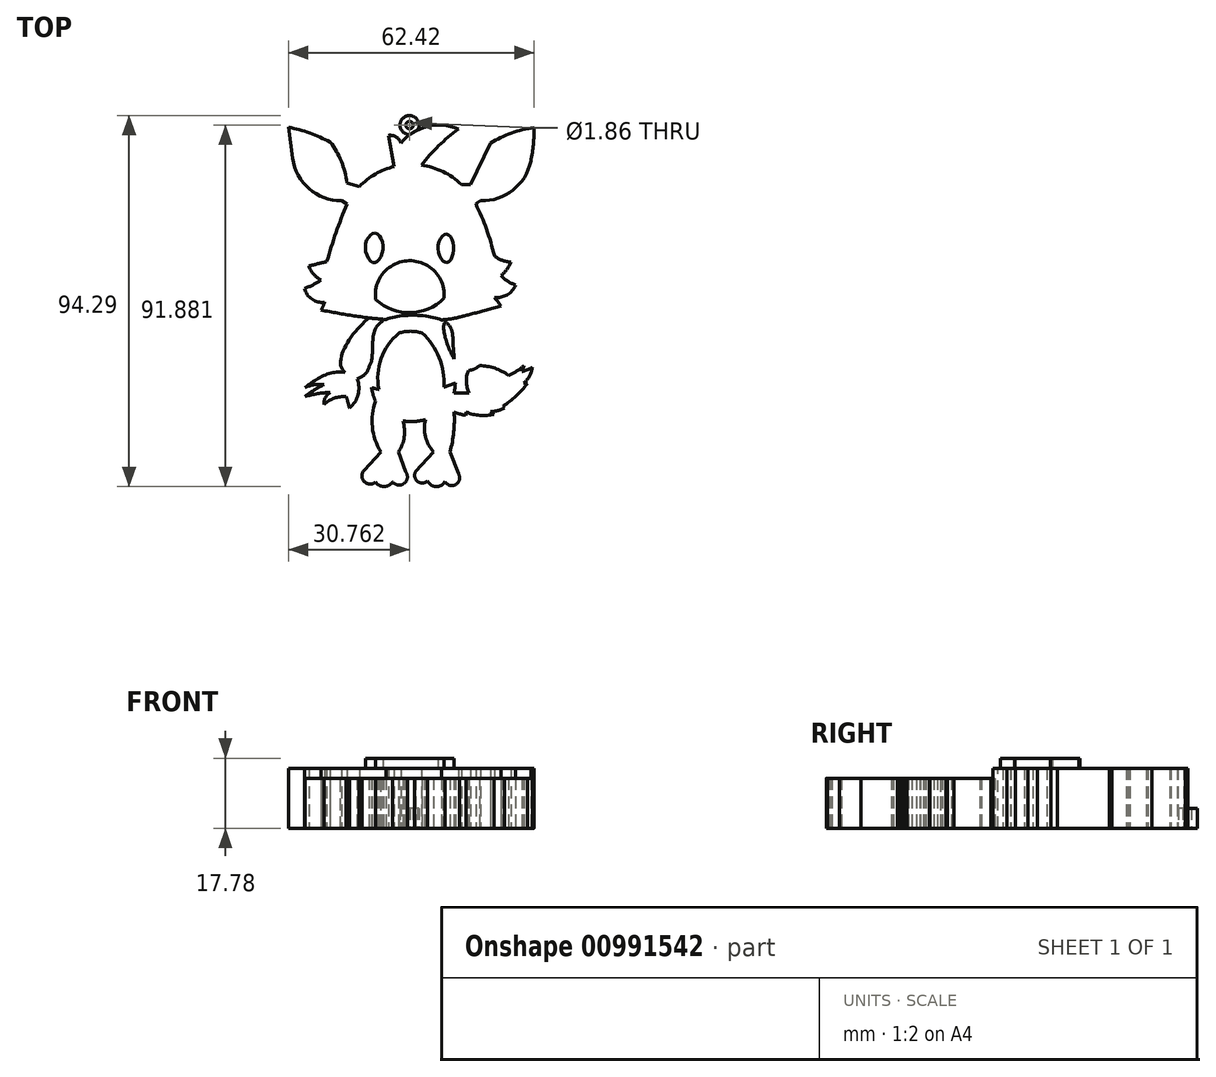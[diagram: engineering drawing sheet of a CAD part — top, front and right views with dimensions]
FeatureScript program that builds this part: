
annotation { "Feature Type Name" : "Feature", "Feature Type Description" : "" }
export const myFeature = defineFeature(function(context is Context, id is Id, definition is map)
    precondition{}
    {
        {
            var Q0;
            Q0=qCreatedBy(makeId("Top.planeOp"),FACE);
            var sketch = newSketch(context, id + "F0", { "sketchPlane" : qUnion([Q0])});
            skLineSegment(sketch, "E0.bottom", {"start": v(-53.94, 80.3) * mm, "end": v(50.51, 80.3) * mm});
            skLineSegment(sketch, "E0.top", {"start": v(-53.94, -54.97) * mm, "end": v(50.51, -54.97) * mm});
            skLineSegment(sketch, "E0.left", {"start": v(-53.94, 80.3) * mm, "end": v(-53.94, -54.97) * mm});
            skLineSegment(sketch, "E0.right", {"start": v(50.51, 80.3) * mm, "end": v(50.51, -54.97) * mm});
            skSolve(sketch);
        }
        {
            var Q0;
            Q0 = qSketchRegion(id + "F0", true);
            extrude(context, id + "F1", {"entities" : qUnion([Q0]), "depth" : 2.54 * mm, "offsetDistance" : 25.4 * mm});
        }
        {
            var Q0;
            Q0=makeQuery(id+"F1.opExtrude","CAP_FACE",FACE,{"disambiguationData":[OSD([sQuery(id+"F0.wireOp",EDGE,"E0.bottom"),sQuery(id+"F0.wireOp",EDGE,"E0.top"),sQuery(id+"F0.wireOp",EDGE,"E0.left"),sQuery(id+"F0.wireOp",EDGE,"E0.right")])],"isStart":false});
            var sketch = newSketch(context, id + "F2", { "sketchPlane" : qUnion([Q0])});
            skLineSegment(sketch, "E1", {"start": v(-10.19, 52.9) * mm, "end": v(-8.72, 45) * mm});
            skArc(sketch, "E2", {"start": v(-6.98, 50.92) * mm, "mid": v(-8.22, 52.5) * mm, "end": v(-10.19, 52.9) * mm});
            skArc(sketch, "E3", {"start": v(7.56, 54.5) * mm, "mid": v(-0.32, 55.19) * mm, "end": v(-6.98, 50.92) * mm});
            skArc(sketch, "E4", {"start": v(7.56, 54.5) * mm, "mid": v(2.55, 50.26) * mm, "end": v(-1.81, 45.35) * mm});
            skArc(sketch, "E5", {"start": v(12, 35.53) * mm, "mid": v(6.3, 42.13) * mm, "end": v(-1.81, 45.35) * mm});
            skArc(sketch, "E6.trimOffspring", {"start": v(-8.72, 45) * mm, "mid": v(-15.79, 41.54) * mm, "end": v(-20.76, 35.43) * mm});
            skLineSegment(sketch, "E7", {"start": v(-20.76, 35.43) * mm, "end": v(-22.08, 36.28) * mm});
            skLineSegment(sketch, "E8", {"start": v(-22.08, 36.28) * mm, "end": v(-20.76, 40.82) * mm});
            skLineSegment(sketch, "E9", {"start": v(-20.76, 40.82) * mm, "end": v(-17.6, 39.9) * mm});
            skLineSegment(sketch, "E10", {"start": v(12, 35.53) * mm, "end": v(13.22, 36.28) * mm});
            skLineSegment(sketch, "E11", {"start": v(13.22, 36.28) * mm, "end": v(10.66, 40.46) * mm});
            skLineSegment(sketch, "E12", {"start": v(10.66, 40.46) * mm, "end": v(8.32, 40.46) * mm});
            skArc(sketch, "E13", {"start": v(-34.54, 47.14) * mm, "mid": v(-30.35, 39.37) * mm, "end": v(-22.08, 36.28) * mm});
            skLineSegment(sketch, "E14", {"start": v(-34.54, 47.14) * mm, "end": v(-35.6, 54.98) * mm});
            skArc(sketch, "E15", {"start": v(-25, 51.2) * mm, "mid": v(-30.16, 53.5) * mm, "end": v(-35.6, 54.98) * mm});
            skArc(sketch, "E16", {"start": v(-20.76, 40.82) * mm, "mid": v(-22.16, 46.3) * mm, "end": v(-25, 51.2) * mm});
            skLineSegment(sketch, "E17", {"start": v(10.66, 40.46) * mm, "end": v(15.68, 50.92) * mm});
            skArc(sketch, "E18", {"start": v(26.82, 54.88) * mm, "mid": v(21.04, 53.48) * mm, "end": v(15.68, 50.92) * mm});
            skArc(sketch, "E19", {"start": v(25.97, 46.38) * mm, "mid": v(26.64, 50.6) * mm, "end": v(26.82, 54.88) * mm});
            skArc(sketch, "E20", {"start": v(13.22, 36.28) * mm, "mid": v(21.44, 39) * mm, "end": v(25.97, 46.38) * mm});
            skArc(sketch, "E21", {"start": v(-30.86, 44.4) * mm, "mid": v(-27.6, 39.12) * mm, "end": v(-21.42, 38.55) * mm});
            skLineSegment(sketch, "E22", {"start": v(-30.86, 44.4) * mm, "end": v(-32.84, 51.2) * mm});
            skArc(sketch, "E23", {"start": v(-25.1, 48.84) * mm, "mid": v(-28.77, 50.69) * mm, "end": v(-32.84, 51.2) * mm});
            skArc(sketch, "E24", {"start": v(-21.14, 39.5) * mm, "mid": v(-22.52, 44.43) * mm, "end": v(-25.1, 48.84) * mm});
            skLineSegment(sketch, "E25", {"start": v(11.32, 39.37) * mm, "end": v(16.43, 48.93) * mm});
            skArc(sketch, "E26", {"start": v(23.89, 51.58) * mm, "mid": v(19.93, 50.9) * mm, "end": v(16.43, 48.93) * mm});
            skLineSegment(sketch, "E27", {"start": v(23.89, 51.58) * mm, "end": v(21.15, 41.38) * mm});
            skArc(sketch, "E28", {"start": v(12.5, 37.45) * mm, "mid": v(17.43, 38.09) * mm, "end": v(21.15, 41.38) * mm});
            skLineSegment(sketch, "E29", {"start": v(-1.94, 54.66) * mm, "end": v(-1.94, 52.52) * mm});
            skLineSegment(sketch, "E30", {"start": v(-1.94, 52.52) * mm, "end": v(-1.03, 52.52) * mm});
            skLineSegment(sketch, "E31", {"start": v(-1.03, 52.52) * mm, "end": v(-1.03, 51.2) * mm});
            skLineSegment(sketch, "E32", {"start": v(-1.03, 51.2) * mm, "end": v(0, 51.2) * mm});
            skLineSegment(sketch, "E33", {"start": v(0, 51.2) * mm, "end": v(0, 49.88) * mm});
            skLineSegment(sketch, "E34", {"start": v(0, 49.88) * mm, "end": v(2.16, 49.88) * mm});
            skArc(sketch, "E35", {"start": v(-20.76, 35.43) * mm, "mid": v(-23.5, 28.19) * mm, "end": v(-25.86, 20.8) * mm});
            skArc(sketch, "E36", {"start": v(16.72, 22.31) * mm, "mid": v(14.72, 29.05) * mm, "end": v(12, 35.53) * mm});
            skArc(sketch, "E37", {"start": v(-25.86, 20.8) * mm, "mid": v(-28.14, 20.28) * mm, "end": v(-30.41, 19.73) * mm});
            skArc(sketch, "E38", {"start": v(-30.41, 19.73) * mm, "mid": v(-29.2, 17.62) * mm, "end": v(-27.27, 16.14) * mm});
            skArc(sketch, "E39", {"start": v(-31.53, 14) * mm, "mid": v(-29.33, 14.94) * mm, "end": v(-27.27, 16.14) * mm});
            skArc(sketch, "E40", {"start": v(-31.53, 14) * mm, "mid": v(-29.63, 11.27) * mm, "end": v(-26.37, 10.53) * mm});
            skArc(sketch, "E41", {"start": v(-27.27, 8.5) * mm, "mid": v(-26.78, 9.5) * mm, "end": v(-26.37, 10.53) * mm});
            skArc(sketch, "E42", {"start": v(16.72, 22.31) * mm, "mid": v(18.67, 21.18) * mm, "end": v(20.89, 20.74) * mm});
            skArc(sketch, "E43", {"start": v(18.42, 17.26) * mm, "mid": v(19.87, 18.85) * mm, "end": v(20.89, 20.74) * mm});
            skArc(sketch, "E44", {"start": v(18.42, 17.26) * mm, "mid": v(20.12, 15.85) * mm, "end": v(22.12, 14.9) * mm});
            skArc(sketch, "E45", {"start": v(16.72, 11.76) * mm, "mid": v(19.97, 12.38) * mm, "end": v(22.12, 14.9) * mm});
            skArc(sketch, "E46", {"start": v(18.42, 9.52) * mm, "mid": v(17.6, 10.66) * mm, "end": v(16.72, 11.76) * mm});
            skFitSpline(sketch, "E47", {"points": [v(-13.57, 28.04) * mm, v(-16.04, 24.9) * mm, v(-13.9, 20.52) * mm, v(-11.55, 24.22) * mm, v(-13.57, 28.04) * mm]});
            skFitSpline(sketch, "E48", {"points": [v(2.37, 24.11) * mm, v(4.5, 27.82) * mm, v(6.4, 24.22) * mm, v(4.61, 20.63) * mm, v(2.37, 24.11) * mm]});
            skArc(sketch, "E49", {"start": v(3.94, 11.54) * mm, "mid": v(-4.95, 21.06) * mm, "end": v(-13.46, 11.2) * mm});
            skArc(sketch, "E50", {"start": v(-13.46, 11.2) * mm, "mid": v(-4.7, 7.88) * mm, "end": v(3.94, 11.54) * mm});
            skArc(sketch, "E51", {"start": v(-9.17, 19.87) * mm, "mid": v(-5.03, 16.55) * mm, "end": v(-1.3, 20.33) * mm});
            skFitSpline(sketch, "E52", {"points": [v(-11.99, 5.47) * mm, v(-14.25, -1.59) * mm, v(-14.72, -8.57) * mm, v(-12.26, -16.6) * mm, v(-4.14, -19.8) * mm, v(4.92, -15.93) * mm, v(6.8, -8.19) * mm, v(6.24, 0) * mm, v(4.25, 5.49) * mm, v(-11.99, 5.47) * mm]});
            skArc(sketch, "E53", {"start": v(6.24, 0) * mm, "mid": v(5.33, 2.77) * mm, "end": v(4.25, 5.49) * mm});
            skFitSpline(sketch, "E54", {"points": [v(9.21, 6.25) * mm, v(11.66, 2.06) * mm, v(13.79, -4.3) * mm, v(10.1, -6.8) * mm, v(6.53, -3.96) * mm, v(4.25, 5.49) * mm, v(8.1, 6.04) * mm, v(9.21, 6.25) * mm]});
            skArc(sketch, "E55", {"start": v(-26.54, -10.42) * mm, "mid": v(-29.04, -10.45) * mm, "end": v(-31.43, -11.15) * mm});
            skArc(sketch, "E56", {"start": v(-26.54, -10.42) * mm, "mid": v(-29.08, -11.8) * mm, "end": v(-31.43, -13.47) * mm});
            skArc(sketch, "E57", {"start": v(-24.97, -12.4) * mm, "mid": v(-28.23, -12.74) * mm, "end": v(-31.43, -13.47) * mm});
            skArc(sketch, "E58", {"start": v(-24.97, -12.4) * mm, "mid": v(-26.21, -13.67) * mm, "end": v(-26.54, -15.41) * mm});
            skArc(sketch, "E59", {"start": v(-20.93, -13.47) * mm, "mid": v(-23.94, -13.87) * mm, "end": v(-26.54, -15.41) * mm});
            skArc(sketch, "E60", {"start": v(-20.1, -16.4) * mm, "mid": v(-20.47, -14.92) * mm, "end": v(-20.93, -13.47) * mm});
            skArc(sketch, "E61", {"start": v(-20.1, -16.4) * mm, "mid": v(-17.93, -13) * mm, "end": v(-18.13, -8.98) * mm});
            skArc(sketch, "E62", {"start": v(10.1, -6.8) * mm, "mid": v(9.74, -10.83) * mm, "end": v(11.68, -14.36) * mm});
            skArc(sketch, "E63", {"start": v(12.52, -11.62) * mm, "mid": v(12.09, -13) * mm, "end": v(11.68, -14.36) * mm});
            skArc(sketch, "E64", {"start": v(17.9, -13.47) * mm, "mid": v(15.29, -12.33) * mm, "end": v(12.52, -11.62) * mm});
            skArc(sketch, "E65", {"start": v(17.9, -13.47) * mm, "mid": v(17.15, -12.02) * mm, "end": v(15.77, -11.15) * mm});
            skArc(sketch, "E66", {"start": v(22, -12.4) * mm, "mid": v(18.94, -11.5) * mm, "end": v(15.77, -11.15) * mm});
            skArc(sketch, "E67", {"start": v(22, -12.4) * mm, "mid": v(20.23, -10.3) * mm, "end": v(17.82, -8.98) * mm});
            skArc(sketch, "E68", {"start": v(22, -9.6) * mm, "mid": v(19.95, -9.03) * mm, "end": v(17.82, -8.98) * mm});
            skArc(sketch, "E69", {"start": v(22, -9.6) * mm, "mid": v(17.87, -6.66) * mm, "end": v(12.92, -5.6) * mm});
            skLineSegment(sketch, "E70", {"start": v(6.48, -12.55) * mm, "end": v(10.35, -12.55) * mm});
            skArc(sketch, "E71", {"start": v(20.33, -8.1) * mm, "mid": v(22.39, -7.01) * mm, "end": v(24.25, -5.62) * mm});
            skArc(sketch, "E72", {"start": v(23.8, -7.08) * mm, "mid": v(25.15, -6.64) * mm, "end": v(26.38, -5.95) * mm});
            skArc(sketch, "E73", {"start": v(24.13, -10.05) * mm, "mid": v(25.64, -8.21) * mm, "end": v(26.38, -5.95) * mm});
            skArc(sketch, "E74", {"start": v(18.86, -15.89) * mm, "mid": v(22.23, -13.3) * mm, "end": v(25.09, -10.16) * mm});
            skArc(sketch, "E75", {"start": v(15.72, -17.3) * mm, "mid": v(17.54, -17.03) * mm, "end": v(19.25, -16.34) * mm});
            skArc(sketch, "E76", {"start": v(9.54, -17.4) * mm, "mid": v(13.06, -18.24) * mm, "end": v(16.67, -17.96) * mm});
            skArc(sketch, "E77", {"start": v(6.45, -17.4) * mm, "mid": v(7.98, -17.9) * mm, "end": v(9.54, -18.22) * mm});
            skLineSegment(sketch, "E78", {"start": v(23.8, -7.08) * mm, "end": v(24.25, -5.62) * mm});
            skLineSegment(sketch, "E79", {"start": v(25.09, -10.16) * mm, "end": v(24.13, -10.05) * mm});
            skLineSegment(sketch, "E80", {"start": v(19.25, -16.34) * mm, "end": v(18.86, -15.89) * mm});
            skLineSegment(sketch, "E81", {"start": v(9.54, -18.22) * mm, "end": v(9.54, -17.4) * mm});
            skLineSegment(sketch, "E82", {"start": v(16.67, -17.96) * mm, "end": v(15.72, -17.3) * mm});
            skArc(sketch, "E83", {"start": v(-14.48, -11.2) * mm, "mid": v(-3.75, -12.34) * mm, "end": v(6.8, -10.04) * mm});
            skArc(sketch, "E84", {"start": v(-1.61, 2.67) * mm, "mid": v(-4.59, 3.13) * mm, "end": v(-7.56, 2.65) * mm});
            skArc(sketch, "E85", {"start": v(-7.56, 2.65) * mm, "mid": v(-12.05, -3.8) * mm, "end": v(-12.63, -11.65) * mm});
            skArc(sketch, "E86", {"start": v(3.9, -11.03) * mm, "mid": v(2.66, -3.57) * mm, "end": v(-1.61, 2.67) * mm});
            skArc(sketch, "E87", {"start": v(-13.5, -14.56) * mm, "mid": v(-14.28, -21.2) * mm, "end": v(-12.13, -27.51) * mm});
            skArc(sketch, "E88", {"start": v(-7.63, -27.52) * mm, "mid": v(-6.19, -23.7) * mm, "end": v(-6.5, -19.65) * mm});
            skArc(sketch, "E89", {"start": v(-12.13, -27.51) * mm, "mid": v(-9.88, -27.92) * mm, "end": v(-7.63, -27.52) * mm});
            skArc(sketch, "E90", {"start": v(-0.82, -19.32) * mm, "mid": v(-0.75, -23.67) * mm, "end": v(1.3, -27.52) * mm});
            skArc(sketch, "E91", {"start": v(5.45, -27.52) * mm, "mid": v(6.52, -20.8) * mm, "end": v(6.04, -14) * mm});
            skArc(sketch, "E92", {"start": v(1.3, -27.52) * mm, "mid": v(3.37, -27.73) * mm, "end": v(5.45, -27.52) * mm});
            skLineSegment(sketch, "E93", {"start": v(-16.41, -32.2) * mm, "end": v(-12.13, -27.51) * mm});
            skLineSegment(sketch, "E94", {"start": v(-7.63, -27.52) * mm, "end": v(-5.87, -32.54) * mm});
            skLineSegment(sketch, "E95", {"start": v(-3.26, -32.48) * mm, "end": v(1.3, -27.52) * mm});
            skLineSegment(sketch, "E96", {"start": v(5.45, -27.52) * mm, "end": v(7.55, -33.01) * mm});
            skArc(sketch, "E97", {"start": v(-3.26, -32.48) * mm, "mid": v(-2.83, -35) * mm, "end": v(-0.27, -34.85) * mm});
            skArc(sketch, "E98", {"start": v(4.17, -35.03) * mm, "mid": v(6.93, -35.8) * mm, "end": v(7.55, -33.01) * mm});
            skArc(sketch, "E99", {"start": v(-0.27, -34.85) * mm, "mid": v(1.9, -36.36) * mm, "end": v(4.17, -35.03) * mm});
            skArc(sketch, "E100", {"start": v(-16.41, -32.2) * mm, "mid": v(-16.34, -35.08) * mm, "end": v(-13.46, -35.13) * mm});
            skArc(sketch, "E101", {"start": v(-9.15, -35.1) * mm, "mid": v(-6.2, -35.5) * mm, "end": v(-5.87, -32.54) * mm});
            skArc(sketch, "E102", {"start": v(-13.46, -35.13) * mm, "mid": v(-11.3, -36.3) * mm, "end": v(-9.15, -35.1) * mm});
            skArc(sketch, "E103", {"start": v(-2.76, 54.3) * mm, "mid": v(-6.1, 57.58) * mm, "end": v(-4.71, 53.11) * mm});
            skCircle(sketch, "E104", {"center": v(-4.84, 55.52) * mm, "radius": 0.93 * mm});
            skLineSegment(sketch, "E105", {"start": v(-12, 5.45) * mm, "end": v(-12, 5.47) * mm});
            skLineSegment(sketch, "E106", {"start": v(-11.99, 5.47) * mm, "end": v(-12, 5.47) * mm});
            skLineSegment(sketch, "E107", {"start": v(-12, 5.48) * mm, "end": v(-12, 5.48) * mm});
            skLineSegment(sketch, "E108", {"start": v(-12, 5.45) * mm, "end": v(-12, 5.48) * mm});
            skLineSegment(sketch, "E109", {"start": v(-12, 5.48) * mm, "end": v(-12, 5.45) * mm});
            skFitSpline(sketch, "E110", {"points": [v(-12, 5.45) * mm, v(-12, 5.48) * mm, v(-12, 5.48) * mm, v(-12, 5.45) * mm]});
            skLineSegment(sketch, "E111", {"start": v(-12, 5.45) * mm, "end": v(-12, 5.49) * mm});
            skPoint(sketch, "E112.orphan", {"position": v(-15.6, 22.27) * mm});
            skPoint(sketch, "E113.orphan", {"position": v(-15.6, 26.48) * mm});
            skPoint(sketch, "E114.end.orphan", {"position": v(-11.96, 26.48) * mm});
            skLineSegment(sketch, "E115", {"start": v(-12, 5.49) * mm, "end": v(-11.38, 6.17) * mm});
            skLineSegment(sketch, "E116", {"start": v(4.25, 5.49) * mm, "end": v(4.07, 6.08) * mm});
            skLineSegment(sketch, "E117", {"start": v(9.21, 6.25) * mm, "end": v(8.71, 6.95) * mm});
            skFitSpline(sketch, "E118", {"points": [v(-27.27, 8.5) * mm, v(-11.38, 6.17) * mm, v(4.07, 6.08) * mm, v(8.71, 6.95) * mm, v(18.42, 9.52) * mm], "startDerivative": vector(50.4, -9.4) * mm, "endDerivative": vector(45.87, 12.2) * mm});
            skFitSpline(sketch, "E119", {"points": [v(-31.43, -11.15) * mm, v(-26.19, -7.95) * mm, v(-21.18, -7.33) * mm, v(-18.13, -8.98) * mm], "startDerivative": vector(13.42, 9.8) * mm, "endDerivative": vector(9.82, -7.27) * mm});
            skFitSpline(sketch, "E120", {"points": [v(-18.13, -8.98) * mm, v(-15.76, -7.33) * mm, v(-14.49, -4.6) * mm, v(-13.07, -3) * mm, v(-13.16, -3) * mm], "startDerivative": vector(8.52, 4.18) * mm, "endDerivative": vector(-2.3, -0.47) * mm});
            skFitSpline(sketch, "E121", {"points": [v(-21.18, -7.33) * mm, v(-22.27, -5.73) * mm, v(-22.08, -3) * mm, v(-20.14, 1.02) * mm, v(-16.51, 5.32) * mm, v(-13.54, 7.77) * mm], "startDerivative": vector(-9.12, 9.92) * mm, "endDerivative": vector(14.04, 10.64) * mm});
            skSolve(sketch);
        }
        {
            var Q0;
            {var subQ0=sQuery(id+"F2.wireOp",EDGE,"E103");Q0=makeQuery(id+"F2.imprint","IMPRINT",FACE,{"disambiguationData":[TD([[makeQuery(id+"F2.imprint","IMPRINT",EDGE,{"derivedFrom":subQ0}),1.0]])]});}
            extrude(context, id + "F3", {"entities" : qUnion([Q0]), "operationType" : NewBodyOperationType.ADD, "depth" : 5.08 * mm, "offsetDistance" : 25.4 * mm});
        }
        {
            var Q0;
            {var subQ0=sQuery(id+"F2.wireOp",EDGE,"E115");Q0=makeQuery(id+"F2.imprint","IMPRINT",FACE,{"disambiguationData":[TD([[makeQuery(id+"F2.imprint","IMPRINT",EDGE,{"derivedFrom":subQ0}),1.0]])]});}
            var Q1;
            {var subQ3=sQuery(id+"F2.wireOp",EDGE,"E55");Q1=makeQuery(id+"F2.imprint","IMPRINT",FACE,{"disambiguationData":[TD([[makeQuery(id+"F2.imprint","IMPRINT",EDGE,{"derivedFrom":subQ3}),-1.0]])]});}
            var Q2;
            {var subQ17=sQuery(id+"F2.wireOp",EDGE,"E53");Q2=makeQuery(id+"F2.imprint","IMPRINT",FACE,{"disambiguationData":[TD([[makeQuery(id+"F2.imprint","IMPRINT",EDGE,{"derivedFrom":subQ17}),1.0]])]});}
            var Q3;
            Q3=makeQuery(id+"F2.imprint","IMPRINT",FACE,{"disambiguationData":[TD([[makeQuery(id+"F2.imprint","IMPRINT",EDGE,{"derivedFrom":sQuery(id+"F2.wireOp",EDGE,"E84")}),1.0]])]});
            var Q4;
            {var subQ6=sQuery(id+"F2.wireOp",EDGE,"E53");Q4=makeQuery(id+"F2.imprint","IMPRINT",FACE,{"disambiguationData":[TD([[makeQuery(id+"F2.imprint","IMPRINT",EDGE,{"derivedFrom":subQ6}),-1.0]])]});}
            var Q5;
            {var subQ3=sQuery(id+"F2.wireOp",EDGE,"E63");Q5=makeQuery(id+"F2.imprint","IMPRINT",FACE,{"disambiguationData":[TD([[makeQuery(id+"F2.imprint","IMPRINT",EDGE,{"derivedFrom":subQ3}),-1.0]])]});}
            var Q6;
            {var subQ0=sQuery(id+"F2.wireOp",EDGE,"E52");var subQ5=sQuery(id+"F2.wireOp",EDGE,"E83");var subQ6=makeQuery(id+"F2.imprint","INTERSECT",VERTEX,{"disambiguationData":[OD(0.0)],"derivedFrom":[subQ0,subQ5]});Q6=makeQuery(id+"F2.imprint","IMPRINT",FACE,{"disambiguationData":[TD([[makeQuery(id+"F2.imprint","IMPRINT",EDGE,{"disambiguationData":[TD([[subQ6,-1.0]])],"derivedFrom":subQ0}),1.0]])]});}
            var Q7;
            {var subQ5=sQuery(id+"F2.wireOp",EDGE,"E63");Q7=makeQuery(id+"F2.imprint","IMPRINT",FACE,{"disambiguationData":[TD([[makeQuery(id+"F2.imprint","IMPRINT",EDGE,{"derivedFrom":subQ5}),1.0]])]});}
            var Q8;
            {var subQ0=sQuery(id+"F2.wireOp",EDGE,"E87");Q8=makeQuery(id+"F2.imprint","IMPRINT",FACE,{"disambiguationData":[TD([[makeQuery(id+"F2.imprint","IMPRINT",EDGE,{"derivedFrom":subQ0}),1.0]])]});}
            var Q9;
            Q9=makeQuery(id+"F2.imprint","IMPRINT",FACE,{"disambiguationData":[TD([[makeQuery(id+"F2.imprint","IMPRINT",EDGE,{"derivedFrom":sQuery(id+"F2.wireOp",EDGE,"E89")}),-1.0]])]});
            var Q10;
            {var subQ3=sQuery(id+"F2.wireOp",EDGE,"E90");Q10=makeQuery(id+"F2.imprint","IMPRINT",FACE,{"disambiguationData":[TD([[makeQuery(id+"F2.imprint","IMPRINT",EDGE,{"derivedFrom":subQ3}),1.0]])]});}
            var Q11;
            Q11=makeQuery(id+"F2.imprint","IMPRINT",FACE,{"disambiguationData":[TD([[makeQuery(id+"F2.imprint","IMPRINT",EDGE,{"derivedFrom":sQuery(id+"F2.wireOp",EDGE,"E92")}),-1.0]])]});
            extrude(context, id + "F4", {"entities" : qUnion([Q0, Q1, Q2, Q3, Q4, Q5, Q6, Q7, Q8, Q9, Q10, Q11]), "operationType" : NewBodyOperationType.ADD, "depth" : 12.7 * mm, "offsetDistance" : 25.4 * mm});
        }
        {
            var Q0;
            {var subQ0=sQuery(id+"F2.wireOp",EDGE,"E13");Q0=makeQuery(id+"F2.imprint","IMPRINT",FACE,{"disambiguationData":[TD([[makeQuery(id+"F2.imprint","IMPRINT",EDGE,{"derivedFrom":subQ0}),1.0]])]});}
            var Q1;
            {var subQ0=sQuery(id+"F2.wireOp",EDGE,"E21");Q1=makeQuery(id+"F2.imprint","IMPRINT",FACE,{"disambiguationData":[TD([[makeQuery(id+"F2.imprint","IMPRINT",EDGE,{"derivedFrom":subQ0}),1.0]])]});}
            var Q2;
            {var subQ3=sQuery(id+"F2.wireOp",EDGE,"E7");Q2=makeQuery(id+"F2.imprint","IMPRINT",FACE,{"disambiguationData":[TD([[makeQuery(id+"F2.imprint","IMPRINT",EDGE,{"derivedFrom":subQ3}),-1.0]])]});}
            var Q3;
            {var subQ4=sQuery(id+"F2.wireOp",EDGE,"E29");Q3=makeQuery(id+"F2.imprint","IMPRINT",FACE,{"disambiguationData":[TD([[makeQuery(id+"F2.imprint","IMPRINT",EDGE,{"derivedFrom":subQ4}),1.0]])]});}
            var Q4;
            {var subQ0=sQuery(id+"F2.wireOp",EDGE,"E17");Q4=makeQuery(id+"F2.imprint","IMPRINT",FACE,{"disambiguationData":[TD([[makeQuery(id+"F2.imprint","IMPRINT",EDGE,{"derivedFrom":subQ0}),-1.0]])]});}
            var Q5;
            {var subQ0=sQuery(id+"F2.wireOp",EDGE,"E25");Q5=makeQuery(id+"F2.imprint","IMPRINT",FACE,{"disambiguationData":[TD([[makeQuery(id+"F2.imprint","IMPRINT",EDGE,{"derivedFrom":subQ0}),-1.0]])]});}
            var Q6;
            {var subQ3=sQuery(id+"F2.wireOp",EDGE,"E10");Q6=makeQuery(id+"F2.imprint","IMPRINT",FACE,{"disambiguationData":[TD([[makeQuery(id+"F2.imprint","IMPRINT",EDGE,{"derivedFrom":subQ3}),1.0]])]});}
            var Q7;
            {var subQ10=sQuery(id+"F2.wireOp",EDGE,"E1");Q7=makeQuery(id+"F2.imprint","IMPRINT",FACE,{"disambiguationData":[TD([[makeQuery(id+"F2.imprint","IMPRINT",EDGE,{"derivedFrom":subQ10}),1.0]])]});}
            extrude(context, id + "F5", {"entities" : qUnion([Q0, Q1, Q2, Q3, Q4, Q5, Q6, Q7]), "operationType" : NewBodyOperationType.ADD, "depth" : 15.24 * mm, "offsetDistance" : 25.4 * mm});
        }
        {
            var Q0;
            Q0=makeQuery(id+"F2.imprint","IMPRINT",FACE,{"disambiguationData":[TD([[makeQuery(id+"F2.imprint","IMPRINT",EDGE,{"derivedFrom":sQuery(id+"F2.wireOp",EDGE,"E47")}),1.0]])]});
            var Q1;
            Q1=makeQuery(id+"F2.imprint","IMPRINT",FACE,{"disambiguationData":[TD([[makeQuery(id+"F2.imprint","IMPRINT",EDGE,{"derivedFrom":sQuery(id+"F2.wireOp",EDGE,"E48")}),-1.0]])]});
            var Q2;
            {var subQ0=sQuery(id+"F2.wireOp",EDGE,"E50");Q2=makeQuery(id+"F2.imprint","IMPRINT",FACE,{"disambiguationData":[TD([[makeQuery(id+"F2.imprint","IMPRINT",EDGE,{"derivedFrom":subQ0}),1.0]])]});}
            var Q3;
            {var subQ0=sQuery(id+"F2.wireOp",EDGE,"E51");Q3=makeQuery(id+"F2.imprint","IMPRINT",FACE,{"disambiguationData":[TD([[makeQuery(id+"F2.imprint","IMPRINT",EDGE,{"derivedFrom":subQ0}),1.0]])]});}
            extrude(context, id + "F6", {"entities" : qUnion([Q0, Q1, Q2, Q3]), "operationType" : NewBodyOperationType.ADD, "depth" : 17.78 * mm, "offsetDistance" : 25.4 * mm});
        }
        {
            var Q0;
            Q0=makeQuery(id+"F1.opExtrude","CAP_FACE",FACE,{"disambiguationData":[OSD([sQuery(id+"F0.wireOp",EDGE,"E0.bottom"),sQuery(id+"F0.wireOp",EDGE,"E0.top"),sQuery(id+"F0.wireOp",EDGE,"E0.left"),sQuery(id+"F0.wireOp",EDGE,"E0.right")])],"isStart":true});
            var Q1;
            {var subQ35=sQuery(id+"F0.wireOp",EDGE,"E0.bottom");var subQ36=makeQuery(id+"F1.opExtrude","SWEPT_FACE",FACE,{"disambiguationData":[OSD([subQ35])]});var subQ49=sQuery(id+"F0.wireOp",EDGE,"E0.top");var subQ52=sQuery(id+"F0.wireOp",EDGE,"E0.left");var subQ55=sQuery(id+"F0.wireOp",EDGE,"E0.right");Q1=makeQuery(id+"F5.boolean.opBoolean","SPLIT",FACE,{"disambiguationData":[TD([subQ36])],"derivedFrom":makeQuery(id+"F4.boolean.opBoolean","SPLIT",FACE,{"disambiguationData":[TD([subQ36])],"derivedFrom":makeQuery(id+"F3.boolean.opBoolean","SPLIT",FACE,{"disambiguationData":[TD([subQ36])],"derivedFrom":makeQuery(id+"F1.opExtrude","CAP_FACE",FACE,{"disambiguationData":[OSD([subQ35,subQ49,subQ52,subQ55])],"isStart":false})})})});}
            extrude(context, id + "F7", {"entities" : qUnion([Q0]), "operationType" : NewBodyOperationType.REMOVE, "endBound" : BoundingType.UP_TO_SURFACE, "oppositeDirection" : true, "depth" : 25.4 * mm, "endBoundEntityFace" : qUnion([Q1]), "offsetDistance" : 25.4 * mm});
        }
    });
